# Revit family: Nuaire_IfcFanType_Isense-plus85
name_source: partatom
category: Mechanical Equipment
revit_build: Autodesk Revit 2018 (Build: 20170223_1515(x64)
units: mm (PartAtom-declared; Revit-internal decimal feet)

## family parameters
Always vertical = Yes
Cut with Voids When Loaded = No
OmniClass Number = 23.75.00.00
OmniClass Title = Climate Control (HVAC)
Part Type = Normal
Room Calculation Point = No
Round Connector Dimension = Use Radius
Shared = No
Work Plane-Based = No

## types (1)
- ISENSE-PLUS
    6 Monthly = SFG20 20-06
    Annually = SFG20 20-06
    Apparent Load = 13.80 VA
    BMS Links = No
    Battery Supply = No
    Bespoke Timeframe = SFG20 20-06
    CE Approval = Yes
    COBie.Type = Yes
    COBie.Type.Area = 0 m²
    COBie.Type.Category = Pr_65_67_29_12 : Centrifugal Fans
    COBie.Type.Description = 230V Continuous Mixed Flow Extract Fan
    COBie.Type.Length = 46 mm  [stored 0.150919 ft]
    COBie.Type.Manufacturer = Nuaire
    COBie.Type.ModelNumber = ISENSE-PLUS
    COBie.Type.ModelReference = ISENSE-PLUS
    COBie.Type.Name = ISENSE-PLUS
    COBie.Type.NominalHeight = 164 mm  [stored 0.538058 ft]
    COBie.Type.NominalLength = 46 mm  [stored 0.150919 ft]
    COBie.Type.NominalWidth = 164 mm  [stored 0.538058 ft]
    COBie.Type.ReplacementCost = 0 $
    COBie.Type.WarrantyDescription = 5 years.  First year parts and labour, remaining 4 years parts only.
    COBie.Type.WarrantyDurationLabor = 1
    COBie.Type.WarrantyDurationParts = 5
    COBie.Type.WarrantyDurationUnit = Year
    COBie.Type.WarrantyGuarantorLabor = Nuaire
    COBie.Type.WarrantyGuarantorParts = Nuaire
    Catalogue Pages = https://www.nuaire.co.uk
    Classification.Uniclass.Pr.Description = Mixed flow fans
    Classification.Uniclass.Pr.Number = Pr_65_67_29_52
    Daily = SFG20 20-06
    Description = 230V Continuous Mixed Flow Extract Fan
    Environmental Product Declaration = WEEE, RoHS
    Fax Number = +44(0)2920-858-222
    Fire Control Panel Links = No
    Frequency = 50.00 Hz
    Full Load Current = 0.060 A
    Height = 164 mm  [stored 0.538058 ft]
    I&M Manual = https://www.nuaire.co.uk
    IFCExportAs = IfcFanType
    IFCExportType = NOTDEFINED
    Length = 46 mm  [stored 0.150919 ft]
    Life Cycle Analysis = 0
    Location of Manufacturer = 51.571856, -3.232638
    Maintenance Required 0 to 300hrs = https://www.nuaire.co.uk
    Maintenance Required 1001 to 2000hrs = https://www.nuaire.co.uk
    Maintenance Required 2001 to 4000hrs = https://www.nuaire.co.uk
    Maintenance Required 301 to 600hrs = https://www.nuaire.co.uk
    Maintenance Required 4001 to 8000hrs = https://www.nuaire.co.uk
    Maintenance Required 601 to 1000hrs = https://www.nuaire.co.uk
    Maintenance Required 8001 to 12000hrs = https://www.nuaire.co.uk
    Manufacturer = Nuaire
    Manufacturer Website = http://www.nuaire.co.uk
    Maximum Ambient Temperature = 40.00 °C
    Model = ISENSE-PLUS
    Monthly = SFG20 20-06
    Nominal Motor Rating = 0.006 kW
    Nominal Motor Speed (rpm) = 2700
    Number of Connection Poles = 2
    OmniClass Number = 23-33 31 19
    OmniClass Title = Fans
    Operation and Maintenance Manual = https://www.nuaire.co.uk
    Postcode = CF83 1NA
    Power Source = Mains
    Product Literature = https://www.nuaire.co.uk
    Product Range = iSense
    Quarterly = SFG20 20-06
    Reference Standard = ISO 9001:2015
    Responsible Sourcing of Materials = FSC
    Revit Family Last Revised = 2023-10-24T12:06:00
    Spigot Diameter = 100 mm  [stored 0.328084 ft]
    Spigot Radius = 50 mm  [stored 0.164042 ft]
    Starting Current = 0.300 A
    Supply Phase = 1
    Telephone Number = +44(0)2920-858-200
    Type Comments = 1
    URL = http://www.nuaire.co.uk
    Voltage = 230.00 V
    Weatherproof or Internal Only = Internal
    Weekly = SFG20 20-06
    Weight = 0.58 kg
    Width = 164 mm  [stored 0.538058 ft]

note: [stored X ft] marks values corroborated as IEEE doubles in the binary element streams (Revit-internal decimal feet)

## geometry (parser evidence)
native form markers: Blend x8, Sweep x16
no freeform markers — native parametric forms only
